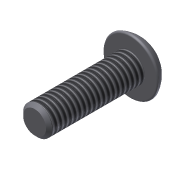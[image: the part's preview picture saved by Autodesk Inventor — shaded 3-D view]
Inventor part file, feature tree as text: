
AUTODESK INVENTOR PART (.ipt)
format: ipt  version: 2011 SP1 (Build 150282100, 282)  size: 125,952 bytes
history: native  units: in
note: dims shown in document units (in); Inventor stores cm internally (conversion verified against a paired STEP export)
features: sketch x3, extrude x2, revolve x1, chamfer x1, thread x1
ambient origin geometry x8: Origin, YZ Plane, XZ Plane, XY Plane, X Axis, Y Axis, Z Axis, Center Point
bodies: Solid1 (feature_tree)
feature tree (8):
  extrude  "Extrusion1"  Depth=0.625in TaperAngle=0.0deg
  revolve  "Revolution1"  [1 undecoded]
  extrude  "Extrusion2"  Depth=0.125in
  chamfer  "Chamfer1"  Distance=0.0625in
  thread  "Thread1"  [1 undecoded]
  sketch  "Sketch1"  dims[d0=0.19in d1=0.625in d2=0.0in]
  sketch  "Sketch2"  dims[d3=0.101in d6=0.08in]
  sketch  "Sketch3"  dims[d7=90.0deg d8=0.125in d9=0.0625in d10=0.0in d12=0.1805in d13=0.02in d14=0.125in d15=45.0deg d16=1.0in d17=0.0in]
note: 2 required parameter values undecoded (feature->parameter linkage not recoverable at this tier; creation-order binding heuristic only, values carry confidence <= 0.55)